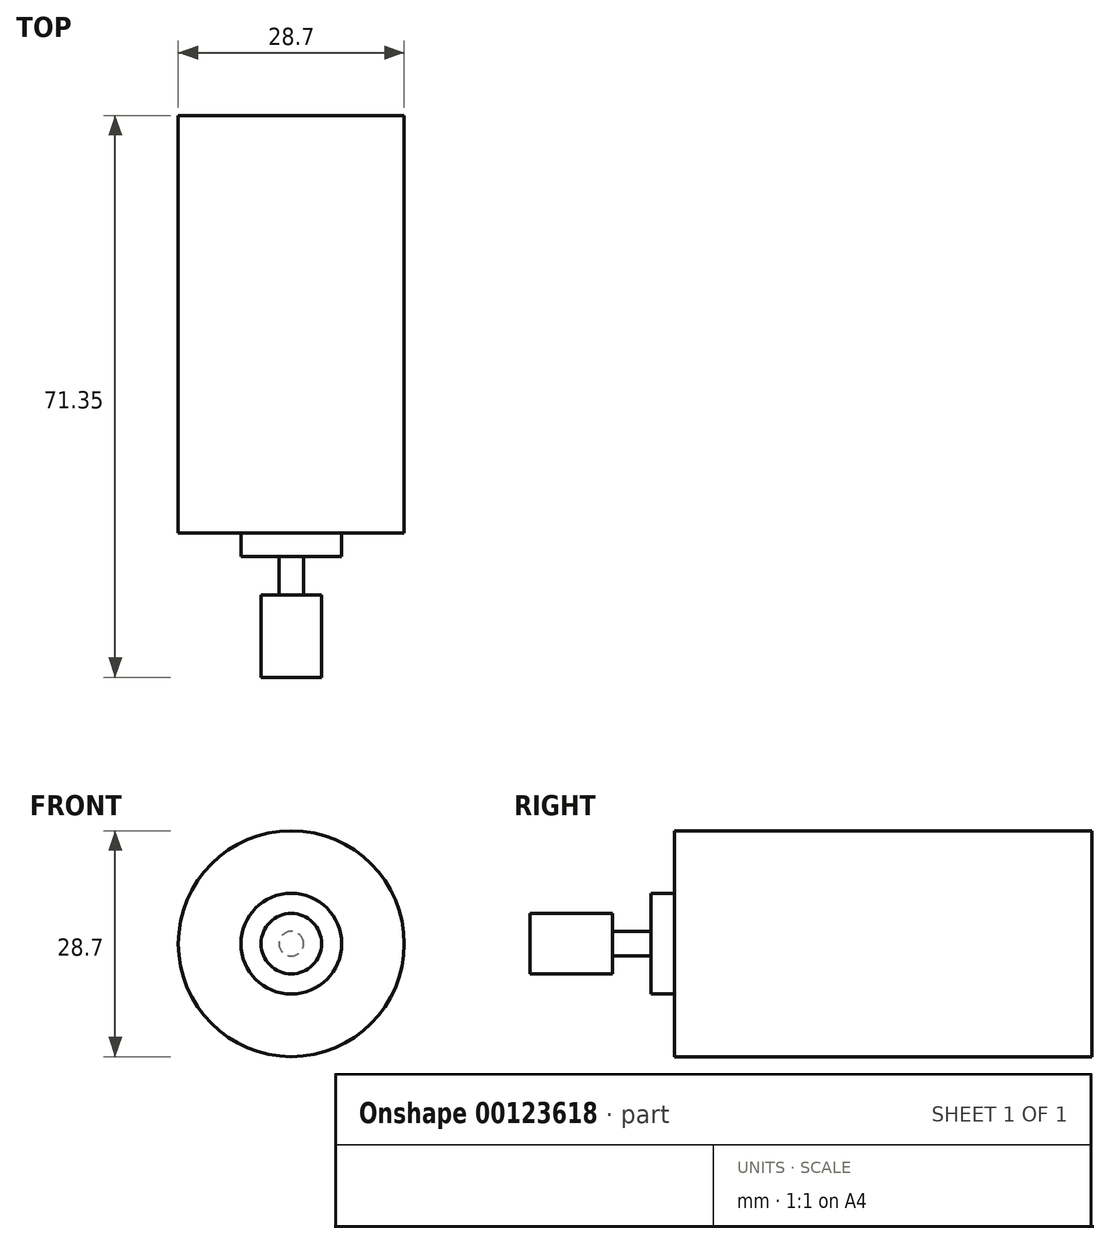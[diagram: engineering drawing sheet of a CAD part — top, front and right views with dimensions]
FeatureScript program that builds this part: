
annotation { "Feature Type Name" : "Feature", "Feature Type Description" : "" }
export const myFeature = defineFeature(function(context is Context, id is Id, definition is map)
    precondition{}
    {
        {
            var Q0;
            Q0=qCreatedBy(makeId("Front.planeOp"),FACE);
            var sketch = newSketch(context, id + "F0", { "sketchPlane" : qUnion([Q0])});
            skCircle(sketch, "E0", {"center": v(0, 0) * mm, "radius": 14.35 * mm});
            skSolve(sketch);
        }
        {
            var Q0;
            Q0=makeQuery(id+"F0.imprint","IMPRINT",FACE,{"disambiguationData":[TD([[makeQuery(id+"F0.imprint","IMPRINT",EDGE,{"derivedFrom":sQuery(id+"F0.wireOp",EDGE,"E0")}),1.0]])]});
            extrude(context, id + "F1", {"entities" : qUnion([Q0]), "depth" : 53 * mm});
        }
        {
            var Q0;
            Q0=makeQuery(id+"F1.opExtrude","CAP_FACE",FACE,{"disambiguationData":[OSD([sQuery(id+"F0.wireOp",EDGE,"E0")])],"isStart":false});
            var sketch = newSketch(context, id + "F2", { "sketchPlane" : qUnion([Q0])});
            skCircle(sketch, "E1", {"center": v(0, 0) * mm, "radius": 6.4 * mm});
            skSolve(sketch);
        }
        {
            var Q0;
            Q0=makeQuery(id+"F2.imprint","IMPRINT",FACE,{"disambiguationData":[TD([[makeQuery(id+"F2.imprint","IMPRINT",EDGE,{"derivedFrom":sQuery(id+"F2.wireOp",EDGE,"E1")}),1.0]])]});
            extrude(context, id + "F3", {"entities" : qUnion([Q0]), "operationType" : NewBodyOperationType.ADD, "depth" : 3 * mm});
        }
        {
            var Q0;
            Q0=makeQuery(id+"F3.opExtrude","CAP_FACE",FACE,{"disambiguationData":[OSD([sQuery(id+"F2.wireOp",EDGE,"E1")])],"isStart":false});
            var sketch = newSketch(context, id + "F4", { "sketchPlane" : qUnion([Q0])});
            skCircle(sketch, "E2", {"center": v(0, 0) * mm, "radius": 1.56 * mm});
            skSolve(sketch);
        }
        {
            var Q0;
            Q0=makeQuery(id+"F4.imprint","IMPRINT",FACE,{"disambiguationData":[TD([[makeQuery(id+"F4.imprint","IMPRINT",EDGE,{"derivedFrom":sQuery(id+"F4.wireOp",EDGE,"E2")}),1.0]])]});
            extrude(context, id + "F5", {"entities" : qUnion([Q0]), "operationType" : NewBodyOperationType.ADD, "depth" : 15.35 * mm});
        }
        {
            var Q0;
            Q0=makeQuery(id+"F5.opExtrude","CAP_FACE",FACE,{"disambiguationData":[OSD([sQuery(id+"F4.wireOp",EDGE,"E2")])],"isStart":false});
            var sketch = newSketch(context, id + "F6", { "sketchPlane" : qUnion([Q0])});
            skCircle(sketch, "E3", {"center": v(0, 0) * mm, "radius": 3.84 * mm});
            skSolve(sketch);
        }
        {
            var Q0;
            Q0=makeQuery(id+"F6.imprint","IMPRINT",FACE,{"disambiguationData":[TD([[makeQuery(id+"F6.imprint","IMPRINT",EDGE,{"derivedFrom":sQuery(id+"F6.wireOp",EDGE,"E3")}),1.0]])]});
            extrude(context, id + "F7", {"entities" : qUnion([Q0]), "operationType" : NewBodyOperationType.ADD, "oppositeDirection" : true, "depth" : 10.48 * mm});
        }
    });
